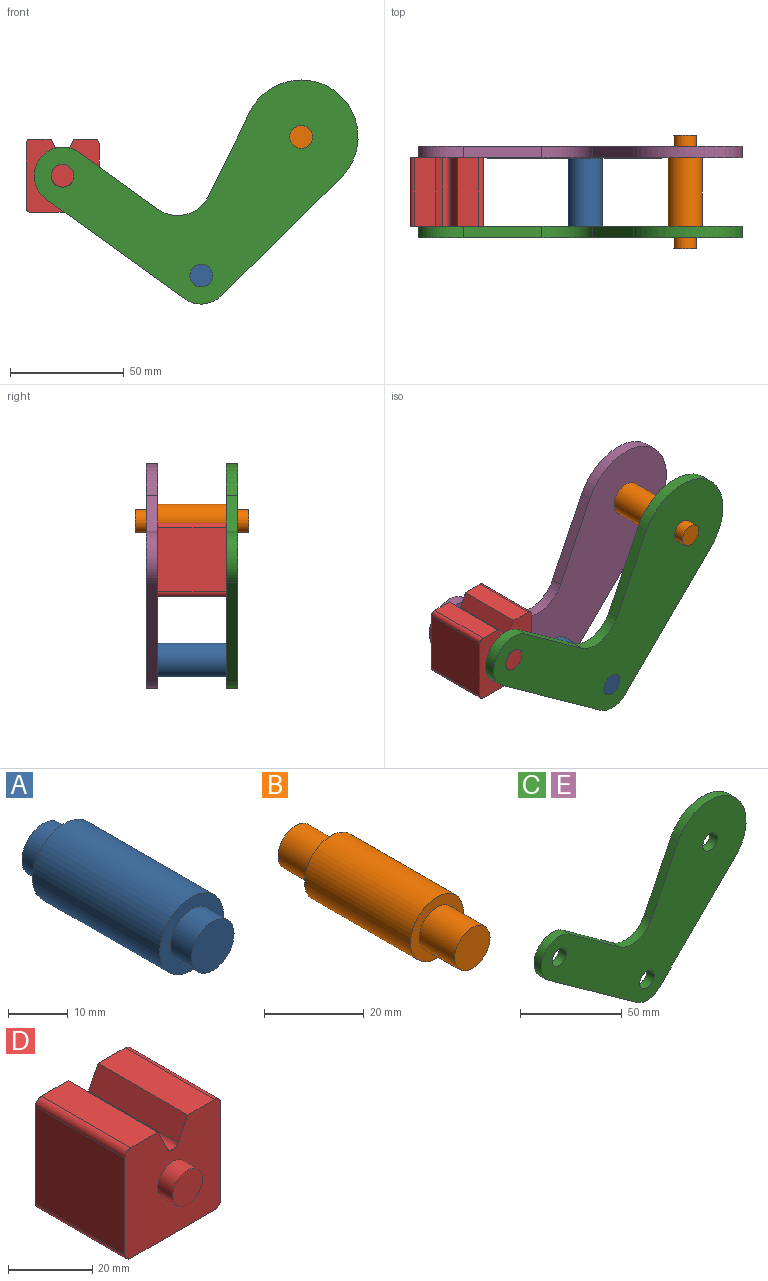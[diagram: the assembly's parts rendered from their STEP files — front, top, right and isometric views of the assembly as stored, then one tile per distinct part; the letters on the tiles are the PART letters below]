
ASSEMBLY  parts=5 mates=4
PART A: 7 faces, bbox 15x40x15 mm
  f0: cylinder r=7.5mm len=30mm, axis (0,-1,0), area 1413.7mm2, adj f2,f5
  f1: cylinder r=5mm len=10mm, axis (0,-1,0), area 157.1mm2, adj f2,f3
  f2: plane 15x15mm, normal (0,-1,0), area 98.2mm2, adj f0,f1
  f3: plane 10x10mm, normal (0,-1,0), area 78.5mm2, adj f1
  f4: cylinder r=5mm len=10mm, axis (0,1,0), area 157.1mm2, adj f5,f6
  f5: plane 15x15mm, normal (0,1,0), area 98.2mm2, adj f0,f4
  f6: plane 10x10mm, normal (0,1,0), area 78.5mm2, adj f4
PART B: 7 faces, bbox 15x50x15 mm
  f0: cylinder r=7.5mm len=30mm, axis (0,-1,0), area 1413.7mm2, adj f2,f5
  f1: cylinder r=5mm len=10mm, axis (0,1,0), area 314.2mm2, adj f2,f3
  f2: plane 15x15mm, normal (0,-1,0), area 98.2mm2, adj f0,f1
  f3: plane 10x10mm, normal (0,-1,0), area 78.5mm2, adj f1
  f4: cylinder r=5mm len=10mm, axis (0,-1,0), area 314.2mm2, adj f5,f6
  f5: plane 15x15mm, normal (0,1,0), area 98.2mm2, adj f0,f4
  f6: plane 10x10mm, normal (0,1,0), area 78.5mm2, adj f4
PART C: 13 faces, bbox 142.2x5x98.4 mm
  f0: plane 52.61x51.97mm, normal (0.7,0,-0.71), area 369.8mm2, adj f1,f9,f11,f12
  f1: cylinder r=25mm len=47.44mm, axis (0,-1,0), area 434.6mm2, adj f0,f2,f11,f12
  f2: plane 37.17x18.26mm, normal (-0.9,0,0.44), area 207.1mm2, adj f1,f3,f11,f12
  f3: cylinder r=15mm len=22.23mm, axis (0,-1,0), area 130.4mm2, adj f2,f4,f11,f12
  f4: plane 34.46x24.81mm, normal (0.58,0,0.81), area 212.3mm2, adj f3,f5,f11,f12
  f5: cylinder r=12.5mm len=22.64mm, axis (0,-1,0), area 196.3mm2, adj f4,f6,f11,f12
  f6: plane 60.86x43.82mm, normal (-0.58,0,-0.81), area 375mm2, adj f5,f9,f11,f12
  f7: cylinder r=5mm len=10mm, axis (0,-1,0), area 157.1mm2, adj f11,f12
  f8: cylinder r=5mm len=10mm, axis (0,-1,0), area 157.1mm2, adj f11,f12
  f9: cylinder r=12.5mm len=16.09mm, axis (0,-1,0), area 87.7mm2, adj f0,f6,f11,f12
  f10: cylinder r=5mm len=10mm, axis (0,-1,0), area 157.1mm2, adj f11,f12
  f11: plane 142.19x98.36mm, normal (0,1,0), area 5739.8mm2, adj f0,f1,f2,f3,f4,f5,f6,f7
  f12: plane 142.19x98.36mm, normal (0,-1,0), area 5739.8mm2, adj f0,f1,f2,f3,f4,f5,f6,f7
PART D: 18 faces, bbox 32.1x40x32.1 mm
  f0: plane 30x6.42mm, normal (0.89,0,0.45), area 215.4mm2, adj f4,f6,f10,f13
  f1: plane 30x6.42mm, normal (-0.89,0,0.45), area 215.4mm2, adj f2,f4,f10,f13
  f2: plane 30x9.04mm, normal (0,0,1), area 271.2mm2, adj f1,f4,f10,f14
  f3: plane 30x28.08mm, normal (1,0,0), area 842.3mm2, adj f4,f10,f14,f15
  f4: plane 32.08x32.08mm, normal (0,-1,0), area 900.6mm2, adj f0,f1,f2,f3,f5,f6,f7,f9
  f5: plane 30x28.08mm, normal (0,0,-1), area 842.3mm2, adj f4,f10,f15,f16
  f6: plane 30x9.04mm, normal (0,0,1), area 271.2mm2, adj f0,f4,f10,f17
  f7: plane 30x28.08mm, normal (-1,0,0), area 842.3mm2, adj f4,f10,f16,f17
  f8: plane 10x10mm, normal (0,-1,0), area 78.5mm2, adj f9
  f9: cylinder r=5mm len=10mm, axis (0,1,0), area 157.1mm2, adj f4,f8
  f10: plane 32.08x32.08mm, normal (0,1,0), area 900.6mm2, adj f0,f1,f2,f3,f5,f6,f7,f12
  f11: plane 10x10mm, normal (0,1,0), area 78.5mm2, adj f12
  f12: cylinder r=5mm len=10mm, axis (0,-1,0), area 157.1mm2, adj f10,f11
  f13: cylinder r=2mm len=30mm, axis (0,1,0), area 132.9mm2, adj f0,f1,f4,f10
  f14: cylinder r=2mm len=30mm, axis (0,1,0), area 94.2mm2, adj f2,f3,f4,f10
  f15: cylinder r=2mm len=30mm, axis (0,-1,0), area 94.2mm2, adj f3,f4,f5,f10
  f16: cylinder r=2mm len=30mm, axis (0,1,0), area 94.2mm2, adj f4,f5,f7,f10
  f17: cylinder r=2mm len=30mm, axis (0,-1,0), area 94.2mm2, adj f4,f6,f7,f10
PART E: same geometry as C
PLACE A t=(0,-20,0)mm
PLACE B t=(0,-20,0)mm fixed
PLACE C t=(0,-20,0)mm
PLACE D t=(0,-20,0)mm
PLACE E t=(0,15,0)mm
MATE fastened C.f1 <-> B.f0  axis (0,1,0) through (0,-15,0)mm
MATE fastened E.f1 <-> B.f0  axis (0,-1,0) through (0,15,0)mm
MATE revolute D.f9 <-> C.f5  axis (0,-1,0) through (-104.69,-20,-17.04)mm
MATE fastened A.f0 <-> C.f7  axis (0,-1,0) through (-43.82,-20,-60.86)mm
